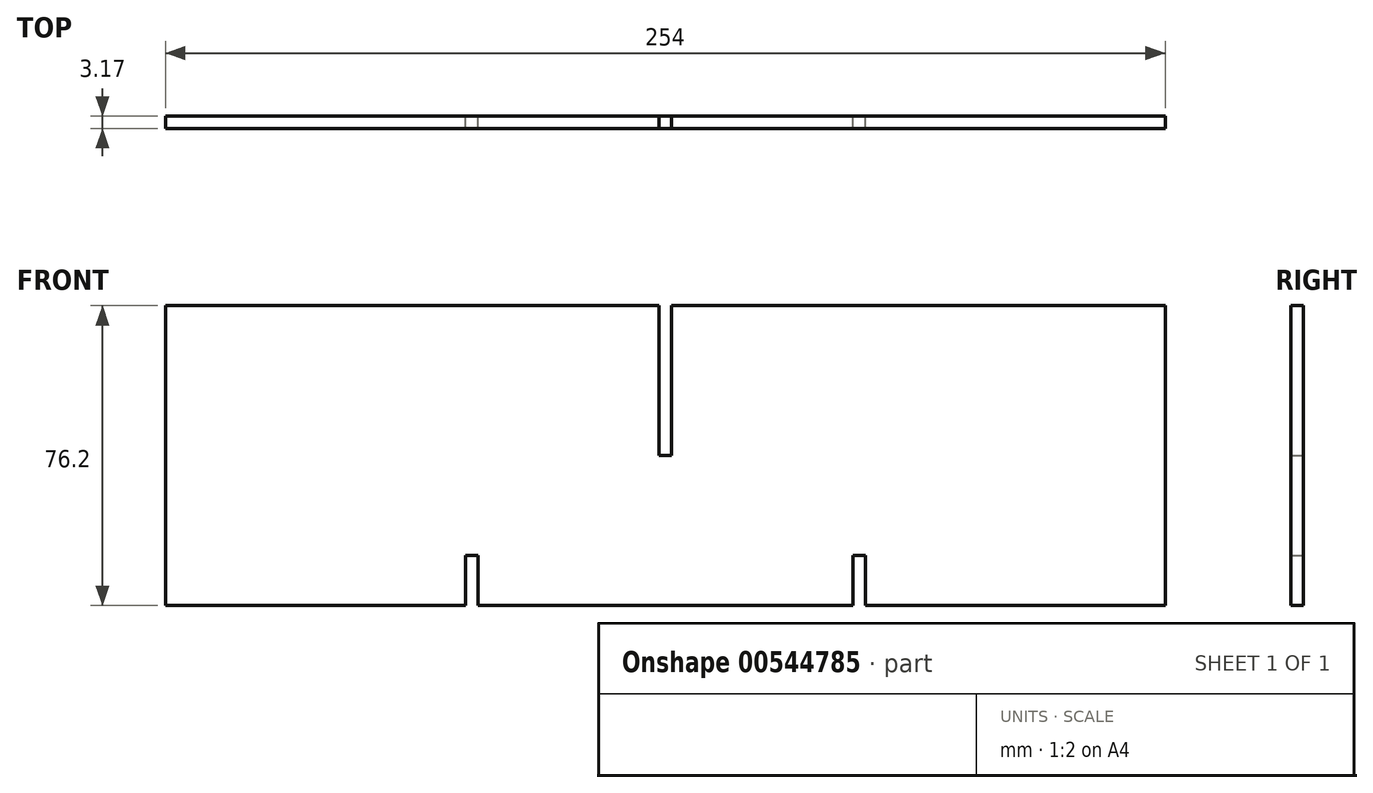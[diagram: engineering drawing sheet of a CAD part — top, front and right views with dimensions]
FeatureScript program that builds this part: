
annotation { "Feature Type Name" : "Feature", "Feature Type Description" : "" }
export const myFeature = defineFeature(function(context is Context, id is Id, definition is map)
    precondition{}
    {
        {
            var Q0;
            Q0=qCreatedBy(makeId("Front.planeOp"),FACE);
            var sketch = newSketch(context, id + "F0", { "sketchPlane" : qUnion([Q0])});
            skLineSegment(sketch, "E0.bottom", {"start": v(-127, 38.1) * mm, "end": v(127, 38.1) * mm});
            skLineSegment(sketch, "E0.top", {"start": v(-127, -38.1) * mm, "end": v(127, -38.1) * mm});
            skLineSegment(sketch, "E0.left", {"start": v(-127, 38.1) * mm, "end": v(-127, -38.1) * mm});
            skLineSegment(sketch, "E0.right", {"start": v(127, 38.1) * mm, "end": v(127, -38.1) * mm});
            skPoint(sketch, "E0.middle", {"position": v(0, 0) * mm});
            skLineSegment(sketch, "E1.bottom", {"start": v(-1.59, 38.1) * mm, "end": v(1.59, 38.1) * mm});
            skLineSegment(sketch, "E1.top", {"start": v(-1.59, 0) * mm, "end": v(1.59, 0) * mm});
            skLineSegment(sketch, "E1.left", {"start": v(-1.59, 38.1) * mm, "end": v(-1.59, 0) * mm});
            skLineSegment(sketch, "E1.right", {"start": v(1.59, 38.1) * mm, "end": v(1.59, 0) * mm});
            skLineSegment(sketch, "E2.bottom", {"start": v(-50.8, -38.1) * mm, "end": v(-47.63, -38.1) * mm});
            skLineSegment(sketch, "E2.top", {"start": v(-50.8, -25.4) * mm, "end": v(-47.63, -25.4) * mm});
            skLineSegment(sketch, "E2.left", {"start": v(-50.8, -38.1) * mm, "end": v(-50.8, -25.4) * mm});
            skLineSegment(sketch, "E2.right", {"start": v(-47.63, -38.1) * mm, "end": v(-47.63, -25.4) * mm});
            skLineSegment(sketch, "E3", {"start": v(0, -38.1) * mm, "end": v(0, -7.8) * mm, "construction": true});
            skLineSegment(sketch, "E4.MirrorCS", {"start": v(47.63, -38.1) * mm, "end": v(47.63, -25.4) * mm});
            skLineSegment(sketch, "E5.MirrorCS", {"start": v(50.8, -25.4) * mm, "end": v(47.63, -25.4) * mm});
            skLineSegment(sketch, "E6.MirrorCS", {"start": v(50.8, -38.1) * mm, "end": v(50.8, -25.4) * mm});
            skLineSegment(sketch, "E7.MirrorCS", {"start": v(50.8, -38.1) * mm, "end": v(47.63, -38.1) * mm});
            skSolve(sketch);
        }
        {
            var Q0;
            {var subQ3=sQuery(id+"F0.wireOp",EDGE,"E0.left");Q0=makeQuery(id+"F0.imprint","IMPRINT",FACE,{"disambiguationData":[TD([[makeQuery(id+"F0.imprint","IMPRINT",EDGE,{"derivedFrom":subQ3}),1.0]])]});}
            extrude(context, id + "F1", {"entities" : qUnion([Q0]), "depth" : 3.17 * mm, "offsetDistance" : 25.4 * mm});
        }
    });
